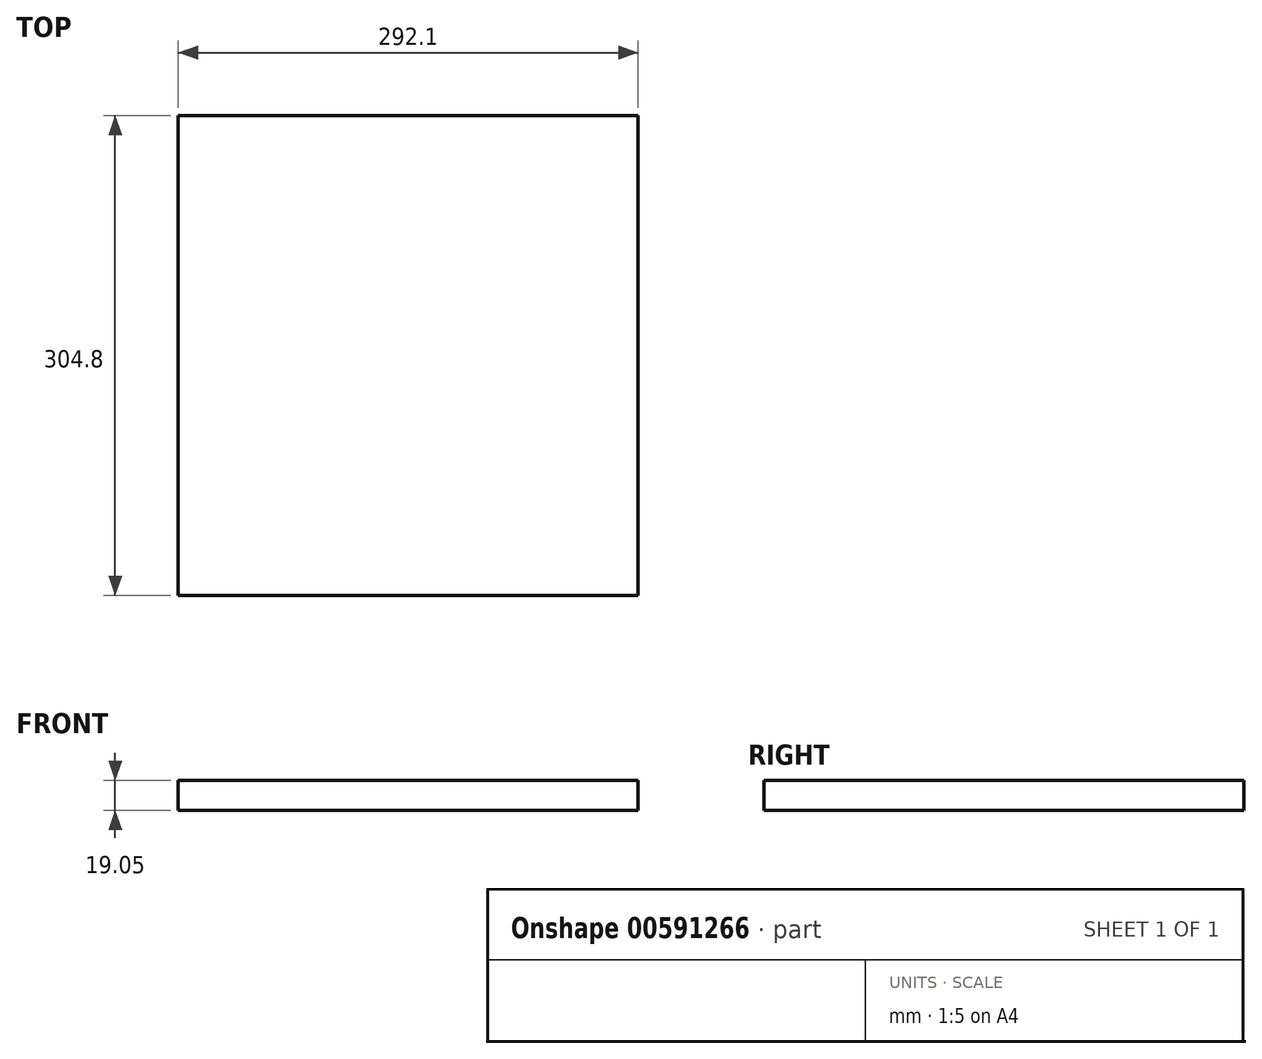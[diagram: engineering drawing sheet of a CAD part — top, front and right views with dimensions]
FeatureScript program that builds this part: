
annotation { "Feature Type Name" : "Feature", "Feature Type Description" : "" }
export const myFeature = defineFeature(function(context is Context, id is Id, definition is map)
    precondition{}
    {
        {
            var Q0;
            Q0=qCreatedBy(makeId("Top.planeOp"),FACE);
            var sketch = newSketch(context, id + "F0", { "sketchPlane" : qUnion([Q0])});
            skLineSegment(sketch, "E0.bottom", {"start": v(146.05, -152.4) * mm, "end": v(-146.05, -152.4) * mm});
            skLineSegment(sketch, "E0.top", {"start": v(146.05, 152.4) * mm, "end": v(-146.05, 152.4) * mm});
            skLineSegment(sketch, "E0.left", {"start": v(146.05, -152.4) * mm, "end": v(146.05, 152.4) * mm});
            skLineSegment(sketch, "E0.right", {"start": v(-146.05, -152.4) * mm, "end": v(-146.05, 152.4) * mm});
            skPoint(sketch, "E0.middle", {"position": v(0, 0) * mm});
            skSolve(sketch);
        }
        {
            var Q0;
            Q0=makeQuery(id+"F0.imprint","IMPRINT",FACE,{"disambiguationData":[TD([[makeQuery(id+"F0.imprint","IMPRINT",EDGE,{"derivedFrom":sQuery(id+"F0.wireOp",EDGE,"E0.bottom")}),-1.0]])]});
            extrude(context, id + "F1", {"entities" : qUnion([Q0]), "depth" : 19.05 * mm, "offsetDistance" : 25.4 * mm});
        }
    });
